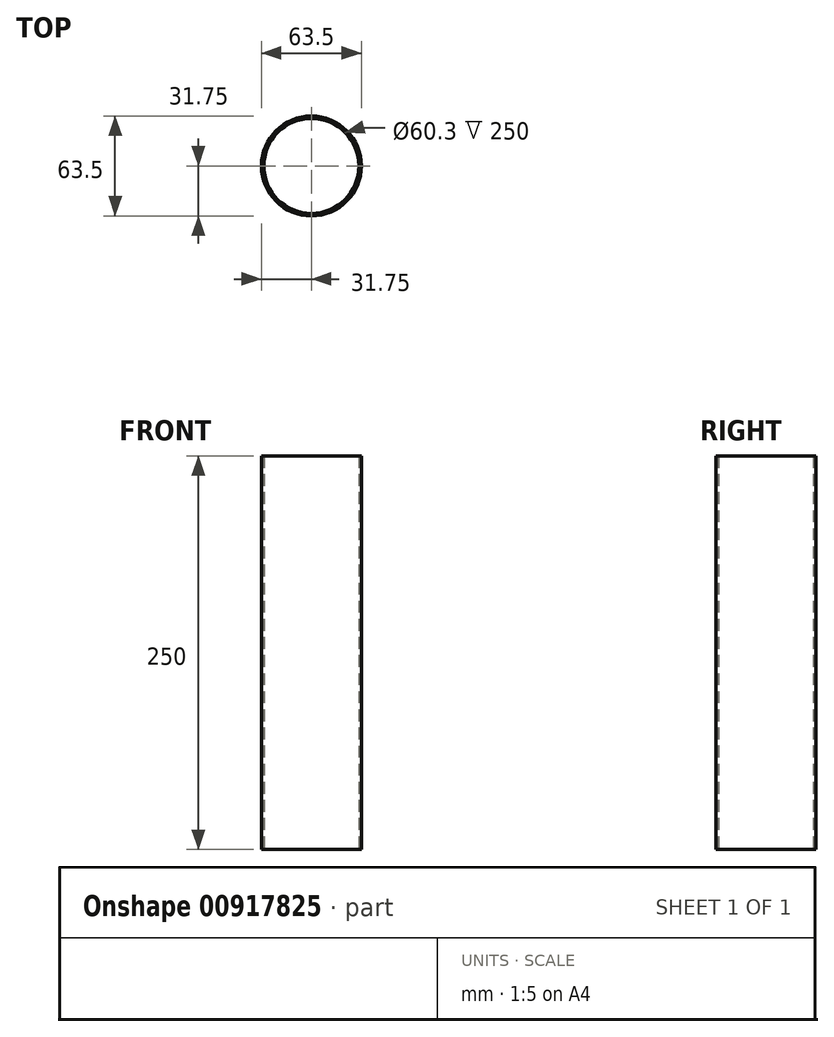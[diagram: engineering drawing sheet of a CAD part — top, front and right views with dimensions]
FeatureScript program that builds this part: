
annotation { "Feature Type Name" : "Feature", "Feature Type Description" : "" }
export const myFeature = defineFeature(function(context is Context, id is Id, definition is map)
    precondition{}
    {
        {
            var Q0;
            Q0=qCreatedBy(makeId("Top.planeOp"),FACE);
            var sketch = newSketch(context, id + "F0", { "sketchPlane" : qUnion([Q0])});
            skCircle(sketch, "E0", {"center": v(0, 0) * mm, "radius": 30.15 * mm});
            skCircle(sketch, "E1", {"center": v(0, 0) * mm, "radius": 31.75 * mm});
            skSolve(sketch);
        }
        {
            var Q0;
            Q0=makeQuery(id+"F0.imprint","IMPRINT",FACE,{"disambiguationData":[TD([[makeQuery(id+"F0.imprint","IMPRINT",EDGE,{"derivedFrom":sQuery(id+"F0.wireOp",EDGE,"E0")}),-1.0]])]});
            extrude(context, id + "F1", {"entities" : qUnion([Q0]), "depth" : 250 * mm, "offsetDistance" : 25 * mm});
        }
    });
